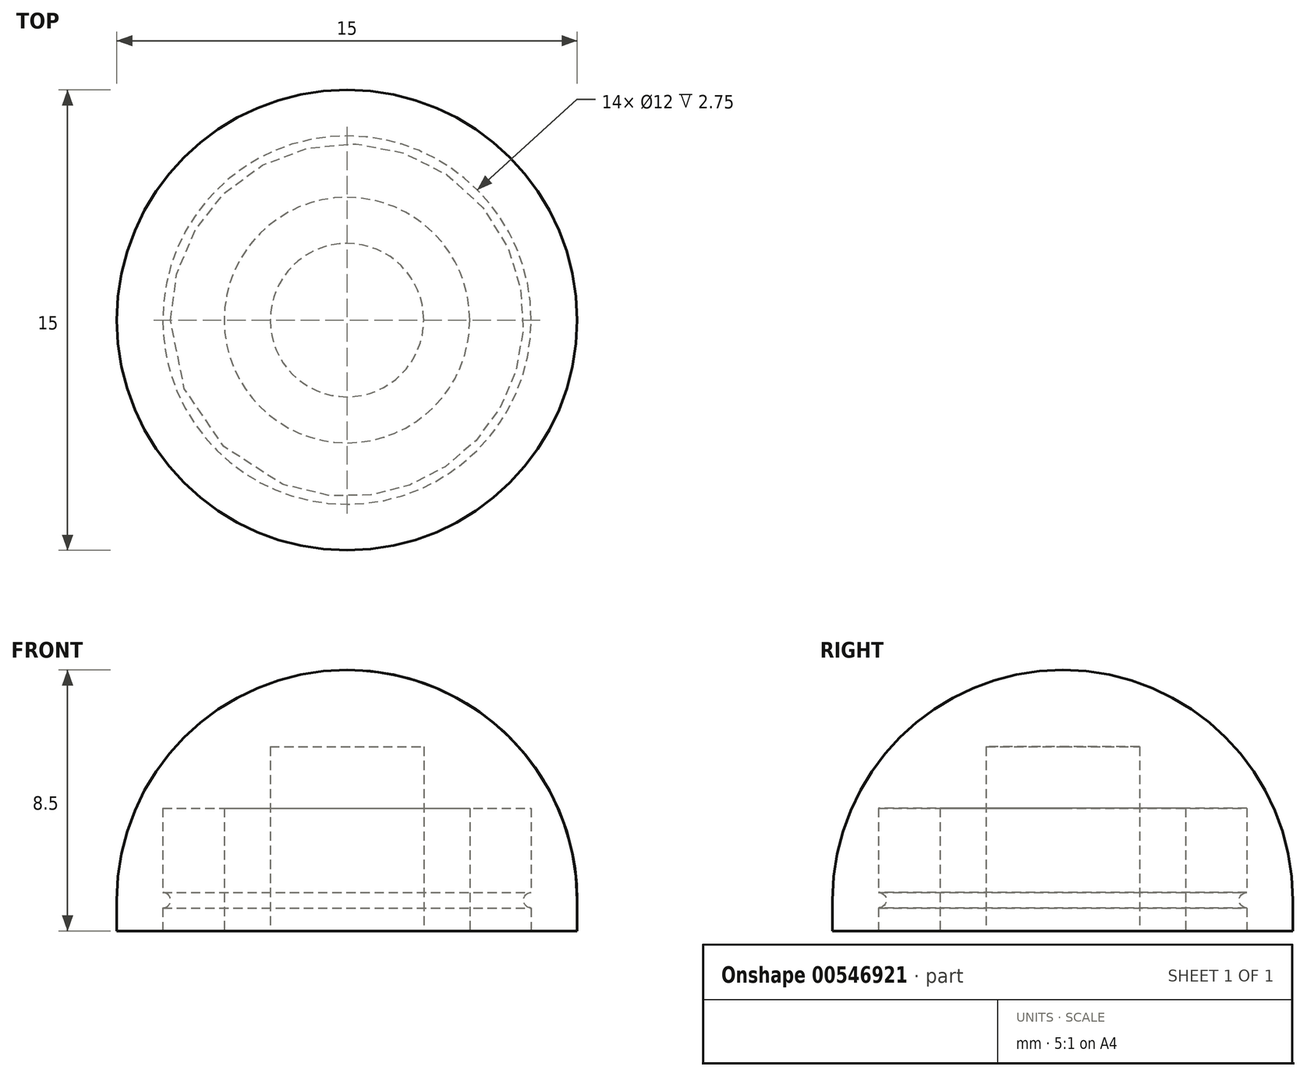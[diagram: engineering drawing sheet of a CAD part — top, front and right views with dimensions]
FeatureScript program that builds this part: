
annotation { "Feature Type Name" : "Feature", "Feature Type Description" : "" }
export const myFeature = defineFeature(function(context is Context, id is Id, definition is map)
    precondition{}
    {
        {
            var Q0;
            Q0=qCreatedBy(makeId("Front.planeOp"),FACE);
            var sketch = newSketch(context, id + "F0", { "sketchPlane" : qUnion([Q0])});
            skLineSegment(sketch, "E0", {"start": v(0, 6) * mm, "end": v(-2.5, 6) * mm});
            skLineSegment(sketch, "E1", {"start": v(-2.5, 6) * mm, "end": v(-2.5, 0) * mm});
            skLineSegment(sketch, "E2", {"start": v(-2.5, 0) * mm, "end": v(-4, 0) * mm});
            skLineSegment(sketch, "E3", {"start": v(-4, 0) * mm, "end": v(-4, 4) * mm});
            skLineSegment(sketch, "E4", {"start": v(-4, 4) * mm, "end": v(-6, 4) * mm});
            skLineSegment(sketch, "E5", {"start": v(-6, 4) * mm, "end": v(-6, 1.25) * mm});
            skLineSegment(sketch, "E6", {"start": v(-6, 0) * mm, "end": v(-7.5, 0) * mm});
            skLineSegment(sketch, "E7", {"start": v(-7.5, 0) * mm, "end": v(-7.5, 1) * mm});
            skLineSegment(sketch, "E8", {"start": v(0, 6) * mm, "end": v(0, 8.5) * mm});
            skArc(sketch, "E9", {"start": v(-7.5, 1) * mm, "mid": v(-5.3, 6.3) * mm, "end": v(0, 8.5) * mm});
            skArc(sketch, "E10", {"start": v(-6, 0.75) * mm, "mid": v(-5.75, 1) * mm, "end": v(-6, 1.25) * mm});
            skLineSegment(sketch, "E11.trimOffspring", {"start": v(-6, 0.75) * mm, "end": v(-6, 0) * mm});
            skSolve(sketch);
        }
        {
            var Q0;
            Q0=makeQuery(id+"F0.imprint","IMPRINT",FACE,{"disambiguationData":[TD([[makeQuery(id+"F0.imprint","IMPRINT",EDGE,{"derivedFrom":sQuery(id+"F0.wireOp",EDGE,"E0")}),-1.0]])]});
            var Q1;
            Q1=sQuery(id+"F0.wireOp",EDGE,"E8");
            revolve(context, id + "F1", {"entities" : qUnion([Q0]), "axis" : qUnion([Q1]), "revolveType" : RevolveType.FULL});
        }
    });
